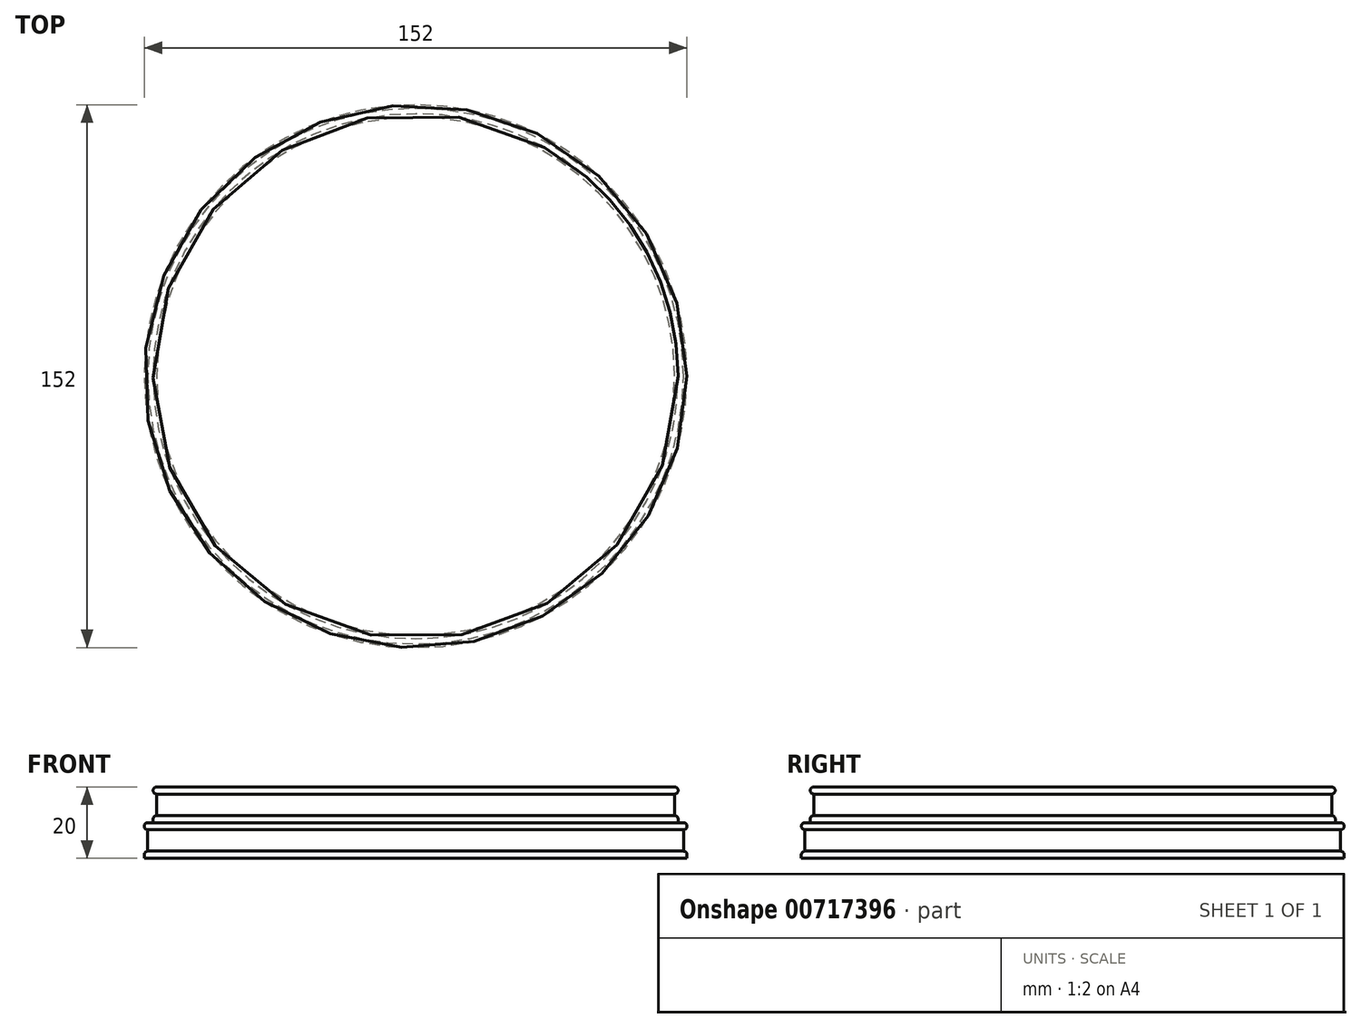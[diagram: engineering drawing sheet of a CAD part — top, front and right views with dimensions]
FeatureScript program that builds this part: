
annotation { "Feature Type Name" : "Feature", "Feature Type Description" : "" }
export const myFeature = defineFeature(function(context is Context, id is Id, definition is map)
    precondition{}
    {
        {
            var Q0;
            Q0=qCreatedBy(makeId("Top.planeOp"),FACE);
            var sketch = newSketch(context, id + "F0", { "sketchPlane" : qUnion([Q0])});
            skCircle(sketch, "E0", {"center": v(0, 0) * mm, "radius": 76 * mm});
            skSolve(sketch);
        }
        {
            var Q0;
            Q0 = qSketchRegion(id + "F0", true);
            extrude(context, id + "F1", {"entities" : qUnion([Q0]), "depth" : 2 * mm, "offsetDistance" : 25 * mm});
        }
        {
            var Q0;
            Q0=makeQuery(id+"F1.opExtrude","CAP_FACE",FACE,{"disambiguationData":[OSD([sQuery(id+"F0.wireOp",EDGE,"E0")])],"isStart":false});
            var sketch = newSketch(context, id + "F2", { "sketchPlane" : qUnion([Q0])});
            skCircle(sketch, "E1", {"center": v(0, 0) * mm, "radius": 75 * mm});
            skSolve(sketch);
        }
        {
            var Q0;
            Q0=makeQuery(id+"F2.imprint","IMPRINT",FACE,{"disambiguationData":[TD([[makeQuery(id+"F2.imprint","IMPRINT",EDGE,{"derivedFrom":sQuery(id+"F2.wireOp",EDGE,"E1")}),1.0]])]});
            extrude(context, id + "F3", {"entities" : qUnion([Q0]), "operationType" : NewBodyOperationType.ADD, "depth" : 6 * mm, "offsetDistance" : 25 * mm});
        }
        {
            var Q0;
            Q0=makeQuery(id+"F3.opExtrude","CAP_FACE",FACE,{"disambiguationData":[OSD([sQuery(id+"F2.wireOp",EDGE,"E1")])],"isStart":false});
            var sketch = newSketch(context, id + "F4", { "sketchPlane" : qUnion([Q0])});
            skCircle(sketch, "E2", {"center": v(0, 0) * mm, "radius": 76 * mm});
            skSolve(sketch);
        }
        {
            var Q0;
            Q0 = qSketchRegion(id + "F4", true);
            var Q1;
            Q1=makeQuery(id+"F4.imprint","IMPRINT",FACE,{"disambiguationData":[TD([[makeQuery(id+"F4.imprint","IMPRINT",EDGE,{"derivedFrom":makeQuery(id+"F3.opExtrude","CAP_EDGE",EDGE,{"disambiguationData":[OSD([sQuery(id+"F2.wireOp",EDGE,"E1")])],"isStart":false})}),1.0]])]});
            extrude(context, id + "F5", {"entities" : qUnion([Q0, Q1]), "operationType" : NewBodyOperationType.ADD, "depth" : 2 * mm, "offsetDistance" : 25 * mm});
        }
        {
            var Q0;
            Q0=makeQuery(id+"F5.opExtrude","CAP_FACE",FACE,{"disambiguationData":[OSD([sQuery(id+"F4.wireOp",EDGE,"E2")])],"isStart":false});
            var sketch = newSketch(context, id + "F6", { "sketchPlane" : qUnion([Q0])});
            skCircle(sketch, "E3", {"center": v(0, 0) * mm, "radius": 73.5 * mm});
            skSolve(sketch);
        }
        {
            var Q0;
            Q0 = qSketchRegion(id + "F6", true);
            extrude(context, id + "F7", {"entities" : qUnion([Q0]), "operationType" : NewBodyOperationType.ADD, "depth" : 2 * mm, "offsetDistance" : 25 * mm});
        }
        {
            var Q0;
            Q0=makeQuery(id+"F7.opExtrude","CAP_FACE",FACE,{"disambiguationData":[OSD([sQuery(id+"F6.wireOp",EDGE,"E3")])],"isStart":false});
            var sketch = newSketch(context, id + "F8", { "sketchPlane" : qUnion([Q0])});
            skCircle(sketch, "E4", {"center": v(0, 0) * mm, "radius": 72.5 * mm});
            skSolve(sketch);
        }
        {
            var Q0;
            Q0 = qSketchRegion(id + "F8", true);
            extrude(context, id + "F9", {"entities" : qUnion([Q0]), "operationType" : NewBodyOperationType.ADD, "depth" : 6 * mm, "offsetDistance" : 25 * mm});
        }
        {
            var Q0;
            Q0=makeQuery(id+"F9.opExtrude","CAP_FACE",FACE,{"disambiguationData":[OSD([sQuery(id+"F8.wireOp",EDGE,"E4")])],"isStart":false});
            var sketch = newSketch(context, id + "F10", { "sketchPlane" : qUnion([Q0])});
            skCircle(sketch, "E5", {"center": v(0, 0) * mm, "radius": 73.5 * mm});
            skSolve(sketch);
        }
        {
            var Q0;
            Q0 = qSketchRegion(id + "F10", true);
            extrude(context, id + "F11", {"entities" : qUnion([Q0]), "operationType" : NewBodyOperationType.ADD, "depth" : 2 * mm, "offsetDistance" : 25 * mm});
        }
        {
            var Q0;
            Q0=makeQuery(id+"F1.opExtrude","CAP_EDGE",EDGE,{"disambiguationData":[OSD([sQuery(id+"F0.wireOp",EDGE,"E0")])],"isStart":false});
            var Q1;
            Q1=makeQuery(id+"F5.opExtrude","CAP_EDGE",EDGE,{"disambiguationData":[OSD([sQuery(id+"F4.wireOp",EDGE,"E2")])],"isStart":true});
            var Q2;
            Q2=makeQuery(id+"F5.opExtrude","CAP_EDGE",EDGE,{"disambiguationData":[OSD([sQuery(id+"F4.wireOp",EDGE,"E2")])],"isStart":false});
            var Q3;
            Q3=makeQuery(id+"F7.opExtrude","CAP_EDGE",EDGE,{"disambiguationData":[OSD([sQuery(id+"F6.wireOp",EDGE,"E3")])],"isStart":true});
            var Q4;
            Q4=makeQuery(id+"F7.opExtrude","CAP_EDGE",EDGE,{"disambiguationData":[OSD([sQuery(id+"F6.wireOp",EDGE,"E3")])],"isStart":false});
            var Q5;
            Q5=makeQuery(id+"F11.opExtrude","CAP_EDGE",EDGE,{"disambiguationData":[OSD([sQuery(id+"F10.wireOp",EDGE,"E5")])],"isStart":true});
            var Q6;
            Q6=makeQuery(id+"F11.opExtrude","CAP_EDGE",EDGE,{"disambiguationData":[OSD([sQuery(id+"F10.wireOp",EDGE,"E5")])],"isStart":false});
            fillet(context, id + "F12", {"entities" : qUnion([Q0, Q1, Q2, Q3, Q4, Q5, Q6]), "radius" : 1 * mm, "tangentPropagation" : true, "allowEdgeOverflow" : false});
        }
    });
